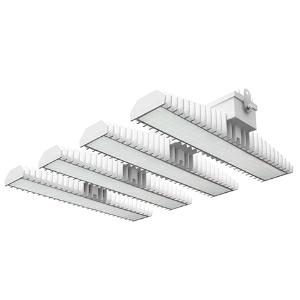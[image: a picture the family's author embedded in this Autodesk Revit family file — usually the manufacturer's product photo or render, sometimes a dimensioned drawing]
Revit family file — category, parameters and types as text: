
# Revit family: 3f_filippi_-_3f_lem_ho_medio_3f_filippi_-_58985_a0812_-_3f_lem_4_ho_led_280_dali_cr_medio___vs_e8b2
name_source: partatom
category: Lighting Fixtures
units: mm (PartAtom-declared; Revit-internal decimal feet)

## family parameters
Cut with Voids When Loaded = No
Host = Face
Light Source = No
Part Type = Normal
Room Calculation Point = No
Round Connector Dimension = Use Diameter
Shared = No

## types (1)
- 3F Filippi - 3F LEM HO Medio (1 x LED, 35835 lm, 276 W, 4000 K)
    Apparent Load = 276 VA
    Approval mark = CE
    CIE Flux Codes = 77 92 98 100 100
    Color Rendering = 80
    Color Temperature = 4000 K
    Control Gear = Electronic transformer
    Default Elevation = 1800 mm
    Description = Industrial luminaire with high light output and high luminous efficiency designed with the most innovative technologies for environments with temperature up to 55°C.

ILLUMINOTECHNICAL
Luminous efficiency 100% (DLOR 98%, ULOR 2%).
Initial luminous flux of the luminaire 35835 lm.
Medium distribution with rectangular shape.
Installation Interdistance Transv.D = 0.87 x hu - Long.D = 0.87 x hu.
Tabular UGR (CIE 117 - 4H-8H; S=0.25H; 70/50/20): RUG 22.2 - 22.2.
Beam angle: 58° - 57°.
Luminous efficacy 130 lm/W.
Lifetime (L93/B10): 30000 h. (tq+25°C)
Lifetime (L90/B10): 50000 h. (tq+25°C)
Lifetime (L85/B10): 80000 h. (tq+25°C)
Lifetime (L80/B10): 100000 h. (tq+25°C)
Lifetime (L85/B10): 50000 h. (tq+55°C)
Sudden decreased luminous flux after 50000 hours: 0% (C0).
Photobiological safety in compliance with IEC/TR 62778: RG0 risk exempt, (IEC 62471).
In compliance with IEC/EN 62722-2-1 - IEC/EN 62717 standards.

SOURCE
4 Mid-Power linear LED modules 70W/840.
Energy efficiency class (UE 2019/2020 - UE 2019/2015): C.
CIE 13.3 Colour rendering index: CRI >80 (R9 <50%).
IES TM-30 Fidelity Index: Rf = 84 Rg = 95.
CCT nominal colour temperature 4000 K.
Colour initial tolerance (MacAdam): SDCM 3.

MECHANICAL
Passive modular heatsinks in die-casted aluminium, painted in white colour.
To optimize the thermal management of the LED module, the heatsinks are oversized and provided with self-cleaning of cooling fins.
Wiring body in aluminium and galvanised steel anchored solidly to the sinks and thermally separated.
3F Lens lenses with high luminous efficiency, transparent methacrylate (PMMA), fixed to the LED modules.
Fixing brackets in stainless steel.
Luminaire with limited surface temperature. - D - (EN 60598-2-24)
Dimensions: 757x542 mm, height 133 mm. Weight 19.74 kg.
IP65 protection degree.
Mechanical strength to impacts IK06 (1 joule).
Glow-wire test resistance 650°C.

ELECTRICAL
Halogen Free DALI-2 DATI (Parts 251, 252, 253), PUSH-DIM, electronic wiring 230V-50/60Hz, power factor 0.97 at full load, THD <25%, constant output current, class I, 2 driver, 2 DALI addresses.
Power of the luminaire 276 W.
ENEC - CE.
SAFE FLICKER: PstLM=<1 and SVM=<0.4 (IEC TR 61547-1 and IEC TR 63158), to ensure a more comfortable and safe light.
Luminaire compliant with EN 60598-2-22 for power supply from a centralised emergency system CPSS (Central Power Supply System), not incorporated in the luminaire - high risk areas excluded. The default power and flux are 100% in AC and 15% in DC.
Ambient temperature from -30°C to +55°C.
Temperature class T6 max 85°C.
Quick connection via M25 5P connector with 9-13 mm tightening range.
Power unit positioned on a separate compartment by the LED module to ensure optimum temperatures of cabling components, to be inspectable and maintainable.
Relative humidity UR: <85%.

INSTALLATION
Ceiling / Suspended / Wall.
All accessories dedicated to this product are available on the Catalog and on our website www.3F-Filippi.com.

ACCESSORIES
A0812 - Anti-glare microprismatic VS moulded glass, tempered, not flammable, with sealing gasket.
One required for each light module. The pack contains 10 pieces.

APPLICATIONS
In commercial environments, exhibition and industrial areas, stores, open areas.
Environments in which it is necessary a total protection against falling fragments (eg environments with foodstuffs or machines with moving parts or with extreme temperature changes), use luminaires with polycarbonate lenses.

LIGHT MANAGEMENT
Recommended minimum setting: 10%.
The luminaire, equipped with (DALI-2 DATI) driver, can be controlled manually with 3F Easy Dim technology or automatically/manually with wired or wireless DALI/D2D control systems.
The D2D driver guarantees interoperability with other devices with the same certification by making the following information available:
Device Data (Part 251), Energy Report (Part 252), Diagnosis & Maintenance (Part 253).
In electrical systems without a regulation system (manual or automatic) and DALI bus, a suitable jumper must be made on the DA-DA terminals of the appliance.

WARNING
Fixture not suitable for cold stores with an ambient temperature <0°C and/or relative humidity >85%.
Luminaire designed for disposal/recycling at end-of-life.
Replaceable (LED only) light source by a professional. Replaceable control gear by a professional.
    Height = 133 mm
    Lamp = 1 x LED
    Lamp Light Flux = 35835 lm
    Lamp Power = 276 W
    Lamp count = 1
    Length = 757 mm
    Lifetime = 50000 h
    Luminous efficacy = 130 lm/W
    Manufacturer = 3F Filippi
    ModVariant = No
    Model = 3F Filippi - 58985+A0812 - 3F LEM 4 HO LED 280 DALI CR MEDIO + VS
    Mounting Place = Ceiling
    Mounting Type = Pendant
    Number of Poles = 1
    OnlyDefault = Yes
    Power Factor = 1
    Product Name = 3F Filippi - 3F LEM HO Medio
    Product group = pendant luminaire
    ProductGroupID = 9
    Protection Class = Protection class I
    Protection Degree = IP 65
    RLX_Detail_Level = 1
    RLX_Emergency_Light_Flux = 0 lm
    RLX_Emergency_Type = 0
    RLX_Emergency_Type_DB = No
    RlxData = <blob elided: 122333 chars, md5=eafeba39>
    Socket = socket
    Standby Power = 0 W
    System Light Flux = 35835 lm
    System Power = 276 W
    Type Comments = Product without accessories
    Type Image = 3f_filippi_-_lem_4__a0812.jpg
    URL = http://relux.com
    VarID = ---
    Voltage = 0 V
    Weight = 0.00 kg
    Width = 542 mm

## geometry (parser evidence)
native form markers: Blend x4, Sweep x13
no freeform markers — native parametric forms only
